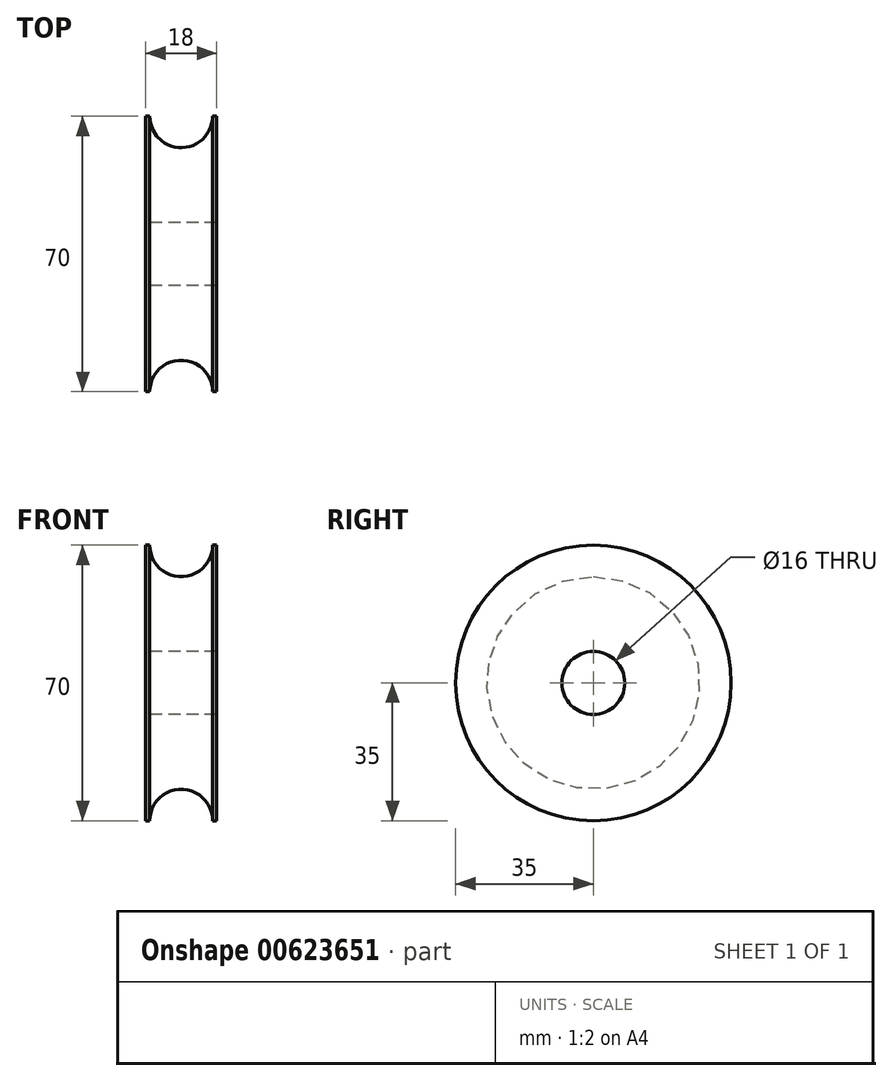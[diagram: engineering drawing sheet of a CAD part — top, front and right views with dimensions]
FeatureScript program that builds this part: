
annotation { "Feature Type Name" : "Feature", "Feature Type Description" : "" }
export const myFeature = defineFeature(function(context is Context, id is Id, definition is map)
    precondition{}
    {
        {
            var Q0;
            Q0=qCreatedBy(makeId("Front.planeOp"),FACE);
            var sketch = newSketch(context, id + "F0", { "sketchPlane" : qUnion([Q0])});
            skLineSegment(sketch, "E0", {"start": v(0, 0) * mm, "end": v(0, 59.65) * mm, "construction": true});
            skLineSegment(sketch, "E1", {"start": v(-9, 8) * mm, "end": v(-9, 35) * mm});
            skLineSegment(sketch, "E2", {"start": v(-9, 35) * mm, "end": v(-8, 35) * mm});
            skLineSegment(sketch, "E3", {"start": v(9, 35) * mm, "end": v(9, 8) * mm});
            skLineSegment(sketch, "E4", {"start": v(-9, 8) * mm, "end": v(9, 8) * mm});
            skLineSegment(sketch, "E5.trimOffspring", {"start": v(8, 35) * mm, "end": v(9, 35) * mm});
            skLineSegment(sketch, "E6", {"start": v(-0.3, 0) * mm, "end": v(21.8, 0) * mm, "construction": true});
            skArc(sketch, "E7", {"start": v(-8, 35) * mm, "mid": v(0, 27) * mm, "end": v(8, 35) * mm});
            skPoint(sketch, "E8", {"position": v(0, 8) * mm});
            skSolve(sketch);
        }
        {
            var Q0;
            Q0=makeQuery(id+"F0.imprint","IMPRINT",FACE,{"disambiguationData":[TD([[makeQuery(id+"F0.imprint","IMPRINT",EDGE,{"derivedFrom":sQuery(id+"F0.wireOp",EDGE,"E1")}),-1.0]])]});
            var Q1;
            Q1=sQuery(id+"F0.wireOp",EDGE,"E6");
            revolve(context, id + "F1", {"entities" : qUnion([Q0]), "axis" : qUnion([Q1]), "revolveType" : RevolveType.FULL});
        }
    });
